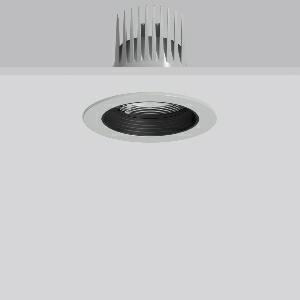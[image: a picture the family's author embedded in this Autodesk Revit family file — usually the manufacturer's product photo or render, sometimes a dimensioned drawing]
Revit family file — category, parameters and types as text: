
# Revit family: heledon_maxi_e_901760_004_1_a0a6
name_source: partatom
category: Lighting Fixtures
units: mm (PartAtom-declared; Revit-internal decimal feet)

## family parameters
Cut with Voids When Loaded = No
Host = Face
Light Source = No
Part Type = Normal
Room Calculation Point = No
Round Connector Dimension = Use Diameter
Shared = No

## types (1)
- HELEDON maxi E (1 x LED Modul 940, 3000 lm, 4000)
    Apparent Load = 25 VA
    Approval mark = CE
    CIE Flux Codes = 97 100 100 100 100
    Color Rendering = 92
    Color Temperature = 4000
    Default Elevation = 1800 mm
    Description = Series: HELEDON maxi
Round recessed downlight. Housing: die-cast aluminium, powder-coated. Black plastic ring and recessed LED to prevent glare from the side. Optical assembly with lens made of plastic (polycarbonate) for the best homogeneous light distribution - can be changed without tools. Best colour rendering index Ra>90. Suitable for Recessed ceiling mounting. Installation without tools thanks to spring fastening system. Including separate LED converter with connecting cable 600 mm.High quality converter without flickering and stroboscopic effect. Through-wiring box (5 pole) available as accessory. The following accessories can be mounted without use of tools: interchangeable lenses, decorative glasses, honeycomb louvre, clear and frosted diffusers, white interchangeable plastic ring. 
Colour: silver
Diameter: 162 mm
Height: 3 mm
Cut-out diameter: 152 mm
Recess height: 200 mm
Luminaire: recess height: 135 mm
Lamp: LED
Socket: without socket
Colour temperature: 4000K
Colour rendering index (CRI): 92
System power: 25 W
Rated luminous flux: 3000 lm
Luminous efficiency: 120 lm/W
Control gear: Regulated power supply
Protection class: II
Type of protection: IP 20
    Height = 0 mm  [stored 0 ft]
    Lamp = 1 x LED Modul 940
    Lamp Light Flux = 3000 lm
    Lamp count = 1
    Length = 162 mm
    Lifetime = 50000 h
    Luminous efficacy = 120 lm/W
    Manufacturer = RZB
    ModVariant = No
    Model = 901760.004.1
    Mounting Place = Ceiling
    Mounting Type = Recessed
    Number of Poles = 1
    OnlyDefault = Yes
    Power Factor = 1
    Product Name = HELEDON maxi E
    Product group = Recessed downlights
    ProductGroupID = 402
    Protection Class = Protection class II
    Protection Degree = IP 20
    RLX_Detail_Level = 1
    RLX_Emergency_Light_Flux = 0 lm
    RLX_Emergency_Type = 0
    RLX_Emergency_Type_DB = No
    RlxData = <blob elided: 118837 chars, md5=c053cc61>
    Socket = socket
    Standby Power = 0 W
    System Light Flux = 3000 lm
    System Power = 25 W
    Type Comments = Product without accessories
    Type Image = 901663.004.jpg
    URL = http://relux.com
    VarID = ---
    Voltage = 230 V
    Voltage Range = 220-240 V
    Weight = 0.00 kg
    Width = 0 mm  [stored 0 ft]

note: [stored X ft] marks values corroborated as IEEE doubles in the binary element streams (Revit-internal decimal feet)

## geometry (parser evidence)
native form markers: Blend x4, Sweep x10
no freeform markers — native parametric forms only
